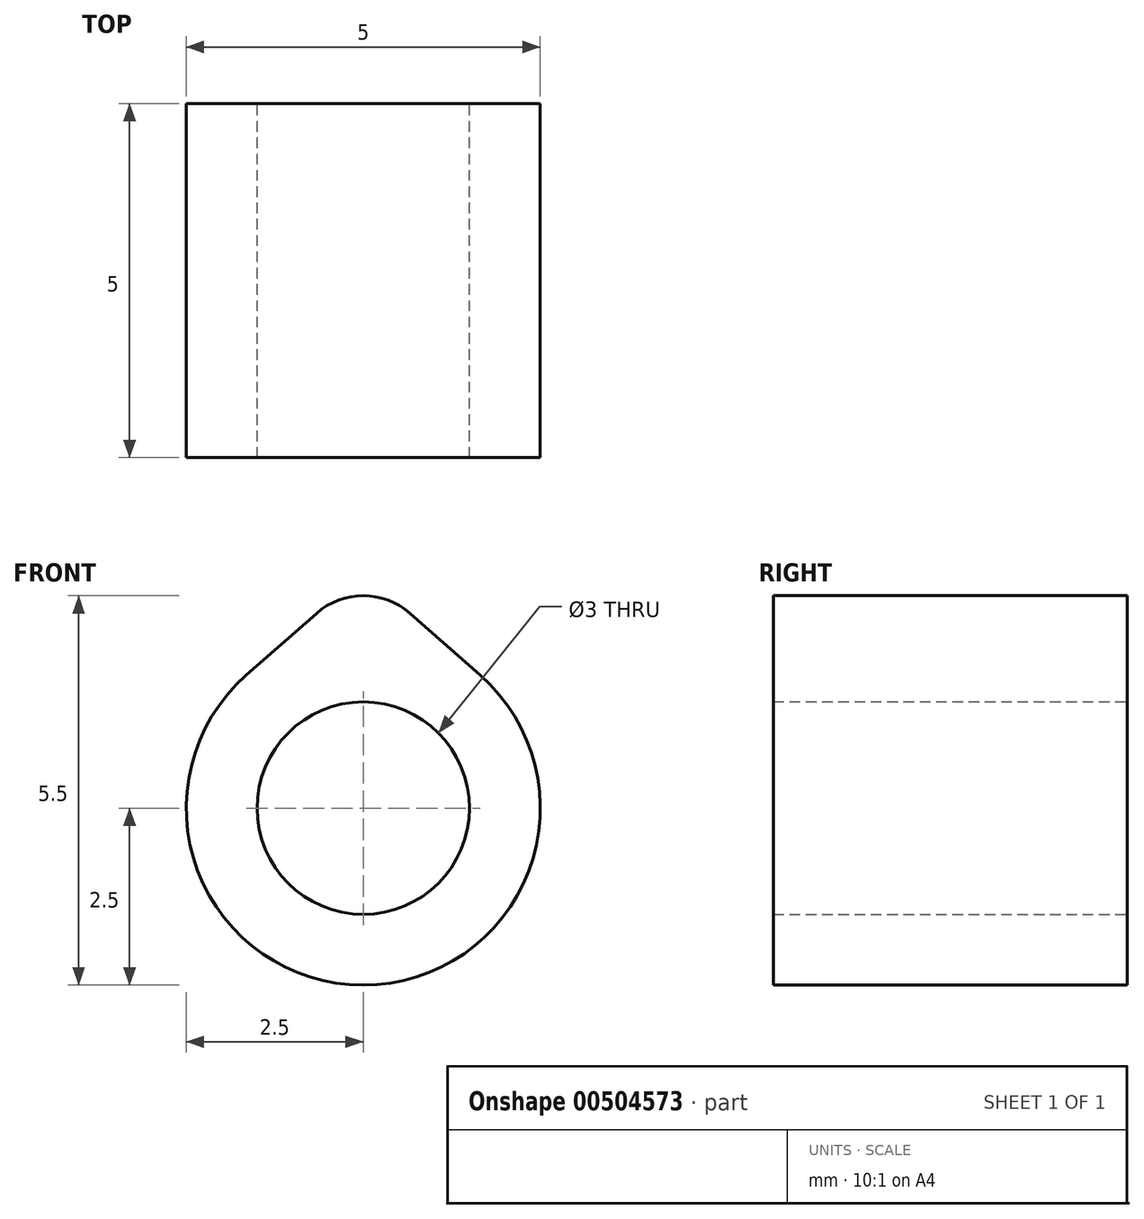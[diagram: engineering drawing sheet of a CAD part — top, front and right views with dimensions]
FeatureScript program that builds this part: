
annotation { "Feature Type Name" : "Feature", "Feature Type Description" : "" }
export const myFeature = defineFeature(function(context is Context, id is Id, definition is map)
    precondition{}
    {
        {
            var Q0;
            Q0=qCreatedBy(makeId("Front.planeOp"),FACE);
            var sketch = newSketch(context, id + "F0", { "sketchPlane" : qUnion([Q0])});
            skCircle(sketch, "E0", {"center": v(0, 0) * mm, "radius": 2.5 * mm});
            skCircle(sketch, "E1", {"center": v(0, 2) * mm, "radius": 1 * mm});
            skLineSegment(sketch, "E2", {"start": v(0.66, 2.75) * mm, "end": v(1.65, 1.87) * mm});
            skLineSegment(sketch, "E3", {"start": v(-0.66, 2.75) * mm, "end": v(-1.65, 1.87) * mm});
            skCircle(sketch, "E4", {"center": v(0, 0) * mm, "radius": 1.5 * mm});
            skSolve(sketch);
        }
        {
            var Q0;
            {var subQ0=sQuery(id+"F0.wireOp",EDGE,"E0");var subQ1=makeQuery(id+"F0.imprint","INTERSECT",VERTEX,{"derivedFrom":[subQ0,sQuery(id+"F0.wireOp",EDGE,"E2")]});Q0=makeQuery(id+"F0.imprint","IMPRINT",FACE,{"disambiguationData":[TD([[makeQuery(id+"F0.imprint","IMPRINT",EDGE,{"disambiguationData":[TD([[subQ1,-1.0]])],"derivedFrom":subQ0}),1.0]])]});}
            var Q1;
            {var subQ0=sQuery(id+"F0.wireOp",EDGE,"E1");var subQ1=sQuery(id+"F0.wireOp",EDGE,"E0");var subQ2=makeQuery(id+"F0.imprint","INTERSECT",VERTEX,{"disambiguationData":[OD(0.0)],"derivedFrom":[subQ1,subQ0]});Q1=makeQuery(id+"F0.imprint","IMPRINT",FACE,{"disambiguationData":[TD([[makeQuery(id+"F0.imprint","IMPRINT",EDGE,{"disambiguationData":[TD([[subQ2,-1.0]])],"derivedFrom":subQ1}),1.0]])]});}
            var Q2;
            {var subQ0=sQuery(id+"F0.wireOp",EDGE,"E1");var subQ1=sQuery(id+"F0.wireOp",EDGE,"E0");var subQ2=makeQuery(id+"F0.imprint","INTERSECT",VERTEX,{"disambiguationData":[OD(0.0)],"derivedFrom":[subQ1,subQ0]});Q2=makeQuery(id+"F0.imprint","IMPRINT",FACE,{"disambiguationData":[TD([[makeQuery(id+"F0.imprint","IMPRINT",EDGE,{"disambiguationData":[TD([[subQ2,-1.0]])],"derivedFrom":subQ1}),-1.0]])]});}
            var Q3;
            {var subQ0=sQuery(id+"F0.wireOp",EDGE,"E2");Q3=makeQuery(id+"F0.imprint","IMPRINT",FACE,{"disambiguationData":[TD([[makeQuery(id+"F0.imprint","IMPRINT",EDGE,{"derivedFrom":subQ0}),-1.0]])]});}
            var Q4;
            {var subQ0=sQuery(id+"F0.wireOp",EDGE,"E3");Q4=makeQuery(id+"F0.imprint","IMPRINT",FACE,{"disambiguationData":[TD([[makeQuery(id+"F0.imprint","IMPRINT",EDGE,{"derivedFrom":subQ0}),1.0]])]});}
            extrude(context, id + "F1", {"entities" : qUnion([Q0, Q1, Q2, Q3, Q4]), "depth" : 5 * mm, "offsetDistance" : 25 * mm});
        }
    });
